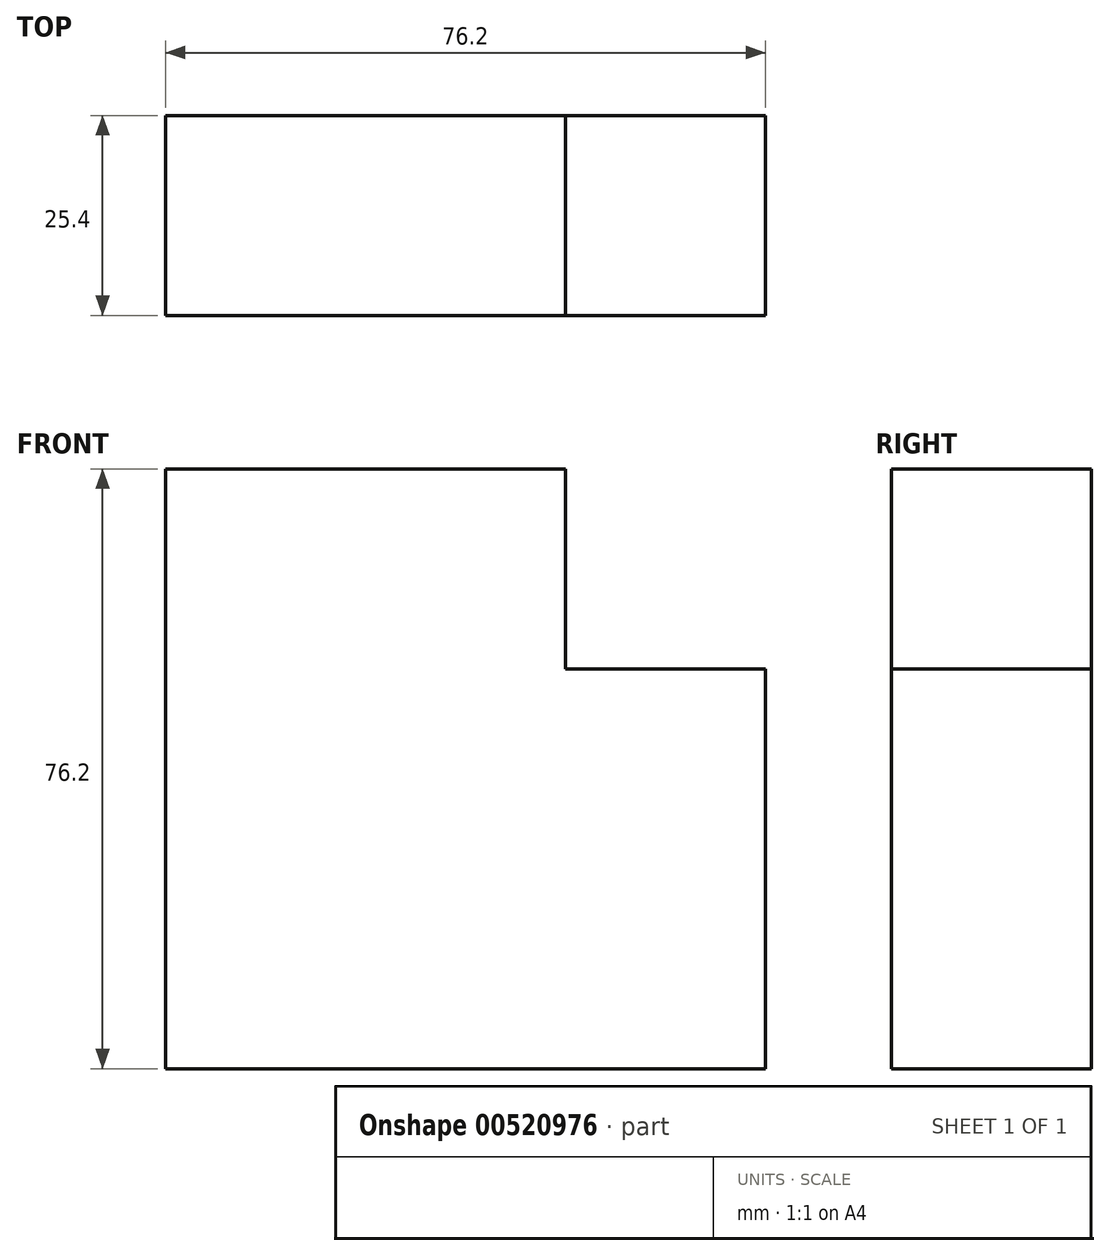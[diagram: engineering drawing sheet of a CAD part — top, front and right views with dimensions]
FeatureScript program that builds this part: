
annotation { "Feature Type Name" : "Feature", "Feature Type Description" : "" }
export const myFeature = defineFeature(function(context is Context, id is Id, definition is map)
    precondition{}
    {
        {
            var Q0;
            Q0=qCreatedBy(makeId("Front.planeOp"),FACE);
            var sketch = newSketch(context, id + "F0", { "sketchPlane" : qUnion([Q0])});
            skLineSegment(sketch, "E0", {"start": v(-76.2, 0) * mm, "end": v(-76.2, -76.2) * mm});
            skLineSegment(sketch, "E1", {"start": v(-76.2, -76.2) * mm, "end": v(0, -76.2) * mm});
            skLineSegment(sketch, "E2", {"start": v(0, -76.2) * mm, "end": v(0, 0) * mm});
            skLineSegment(sketch, "E3", {"start": v(0, 0) * mm, "end": v(-76.2, 0) * mm});
            skSolve(sketch);
        }
        {
            var Q0;
            Q0=makeQuery(id+"F0.imprint","IMPRINT",FACE,{"disambiguationData":[TD([[makeQuery(id+"F0.imprint","IMPRINT",EDGE,{"derivedFrom":sQuery(id+"F0.wireOp",EDGE,"E0")}),1.0]])]});
            extrude(context, id + "F1", {"entities" : qUnion([Q0]), "depth" : 25.4 * mm, "offsetDistance" : 25.4 * mm});
        }
        {
            var Q0;
            Q0=qCreatedBy(makeId("Front.planeOp"),FACE);
            var sketch = newSketch(context, id + "F2", { "sketchPlane" : qUnion([Q0])});
            skLineSegment(sketch, "E4", {"start": v(-25.4, 0) * mm, "end": v(-25.4, -25.4) * mm});
            skLineSegment(sketch, "E5", {"start": v(-25.4, -25.4) * mm, "end": v(0, -25.4) * mm});
            skLineSegment(sketch, "E6", {"start": v(0, -25.4) * mm, "end": v(0, 0) * mm});
            skLineSegment(sketch, "E7", {"start": v(0, 0) * mm, "end": v(-25.4, 0) * mm});
            skSolve(sketch);
        }
        {
            var Q0;
            Q0 = qSketchRegion(id + "F2", true);
            extrude(context, id + "F3", {"entities" : qUnion([Q0]), "operationType" : NewBodyOperationType.REMOVE, "depth" : 25.4 * mm, "offsetDistance" : 25.4 * mm});
        }
    });
